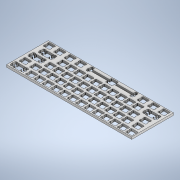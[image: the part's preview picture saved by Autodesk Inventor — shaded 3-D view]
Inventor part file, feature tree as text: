
AUTODESK INVENTOR PART (.ipt)
format: ipt  version: 2022 (Build 260153000, 153)  size: 1,647,104 bytes
history: native  units: in
note: dims shown in document units (in); Inventor stores cm internally (conversion verified against a paired STEP export)
features: extrude x1, sketch x1
ambient origin geometry x8: Origin, YZ Plane, XZ Plane, XY Plane, X Axis, Y Axis, Z Axis, Center Point
bodies: Solid1 (feature_tree)
feature tree (2):
  extrude  "Extrusion1"  [1 undecoded]
  sketch  "Sketch1"  dims[d0=0.2in d1=0.0in]
note: 1 required parameter value undecoded (feature->parameter linkage not recoverable at this tier; creation-order binding heuristic only, values carry confidence <= 0.55)
